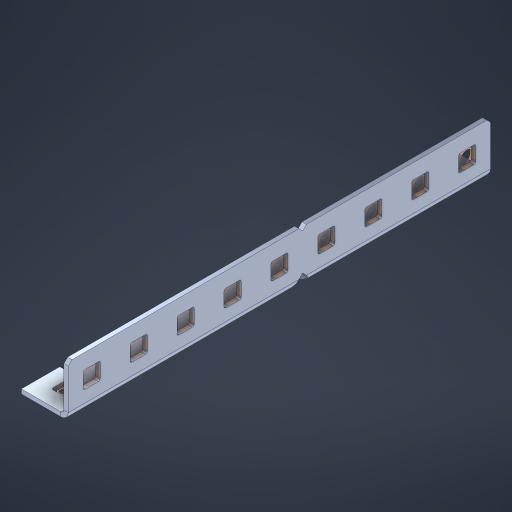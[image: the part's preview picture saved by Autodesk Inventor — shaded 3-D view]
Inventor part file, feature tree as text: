
AUTODESK INVENTOR PART (.ipt)
format: ipt  version: 2023 (Build 270158000, 158)  size: 642,560 bytes
history: native  units: in
note: dims shown in document units (in); Inventor stores cm internally (conversion verified against a paired STEP export)
features: other x34, extrude x25, sheet_metal_op x11, sketch x10, pattern_linear x2, mirror x1, chamfer x1
ambient origin geometry x8: Origin, YZ Plane, XZ Plane, XY Plane, X Axis, Y Axis, Z Axis, Center Point
bodies: Solid1 (feature_tree), Body (feature_tree)
feature tree (84):
  sheet_metal_op  "Flanges"
  other  "Flange Pattern Plane"
  other  "Flange Pattern Sketch"
  sheet_metal_op  "Flange Pattern"
  sheet_metal_op  "Body Pattern"
  pattern_linear  "Center Pattern"  Spacing1=0.0469in  [1 undecoded]
  other  "Arc Length"
  mirror  "Notch Mirror"
  pattern_linear  "Notch Pattern"  Spacing1=0.182in  [1 undecoded]
  chamfer  "End Chamfer"
  extrude  "Half Cut"  Depth=0.02in
  sketch  "Sketch1"  dims[d0=1.0in]
  other  "Plate1"
  sketch  "Sketch2"  dims[d1=4.5in]
  other  "Plate2"
  sheet_metal_op  "Bend1"
  sheet_metal_op  "Corner1"
  sketch  "Sketch3"  dims[d2=0.0469in]
  sketch  "Sketch7"  dims[d3=0.0469in]
  other  "Srf1"
  other  "Srf2"
  sketch  "Sketch8"  dims[d4=0.0234in]
  sketch  "Sketch9"  dims[d5=0.0938in]
  other  "Srf91"
  sheet_metal_op  "Body Pattern Sketch"
  other  "Srf92"
  sketch  "Sketch13"  dims[d6=0.0469in]
  sketch  "Sketch14"  dims[d7=0.5in d8=90.0deg d9=0.0312in]
  sketch  "Sketch15"  dims[d10=0.1875in]
  sketch  "Sketch16"  dims[d11=0.0469in d12=0.0469in d16=0.182in d17=0.02in d18=0.0469in d19=0.0in d20=0.25in d21=0.25in d38=3.5433in d40=0.5in d41=0.3937in d43=1.0in d46=0.172in d47=1.0in d48=0.0in d49=0.182in d50=0.02in d51=0.25in d52=0.25in d53=0.0469in d54=0.0in d55=0.172in d56=1.0in d57=0.0in d58=0.25in d60=3.5433in d62=0.5in d63=0.3937in d65=0.5in d85=0.1227in d86=0.1659in d88=0.04in d89=0.0469in d90=0.0in d91=0.04in d92=0.0491in d95=2.5in d96=0.04in d97=0.25in d98=45.0deg d99=0.25in d100=0.5in d101=0.0in d102=2.497in d106=0.182in d107=0.02in d108=0.5in d109=0.5in d110=0.0469in d111=0.0in d112=0.172in d113=0.5in d114=0.0in d117=0.5in d118=0.5in d119=0.5in]
  other  "Srf786"
  other  "Srf823"
  other  "Srf824"
  other  "Srf825"
  other  "Srf826"
  other  "Srf827"
  other  "Srf828"
  other  "Srf829"
  other  "Srf856"
  other  "Srf857"
  other  "Srf858"
  other  "Srf859"
  other  "Srf860"
  other  "Srf861"
  other  "Srf862"
  other  "Srf889"
  other  "Srf890"
  other  "Srf891"
  other  "Srf892"
  other  "Srf893"
  other  "Srf894"
  other  "Srf895"
  other  "Srf896"
  sheet_metal_op  "Flange Stamp"
  sheet_metal_op  "Flange Circle"
  sheet_metal_op  "Body Stamp"
  sheet_metal_op  "Body Circle"
  other  "Center Stamp"
  other  "Center Circle"
  sheet_metal_op  "Notch"
  extrude  "ExtrusionSrf2"  Depth=0.0469in
  extrude  "ExtrusionSrf92"  TaperAngle=0.0deg  [1 undecoded]
  extrude  "ExtrusionSrf823"  Depth=0.5in
  extrude  "ExtrusionSrf824"  Depth=0.5in
  extrude  "ExtrusionSrf825"  Depth=0.5in
  extrude  "ExtrusionSrf826"  Depth=0.5in
  extrude  "ExtrusionSrf827"  Depth=1.0in TaperAngle=0.0deg
  extrude  "ExtrusionSrf828"  Depth=0.182in
  extrude  "ExtrusionSrf829"  Depth=0.02in
  extrude  "ExtrusionSrf856"  Depth=0.5in
  extrude  "ExtrusionSrf857"  Depth=0.5in
  extrude  "ExtrusionSrf858"  Depth=0.0469in
  extrude  "ExtrusionSrf859"  TaperAngle=0.0deg  [1 undecoded]
  extrude  "ExtrusionSrf860"  Depth=0.5in
  extrude  "ExtrusionSrf861"  Depth=1.0in TaperAngle=0.0deg
  extrude  "ExtrusionSrf862"  Depth=0.5in
  extrude  "ExtrusionSrf889"  Depth=0.5in
  extrude  "ExtrusionSrf890"  Depth=0.5in
  extrude  "ExtrusionSrf891"  Depth=0.5in
  extrude  "ExtrusionSrf892"  Depth=0.5in
  extrude  "ExtrusionSrf893"  Depth=0.5in
  extrude  "ExtrusionSrf894"  Depth=0.0469in
  extrude  "ExtrusionSrf895"  TaperAngle=0.0deg  [1 undecoded]
  extrude  "ExtrusionSrf896"  Depth=0.5in
note: 5 required parameter values undecoded (feature->parameter linkage not recoverable at this tier; creation-order binding heuristic only, values carry confidence <= 0.55)
